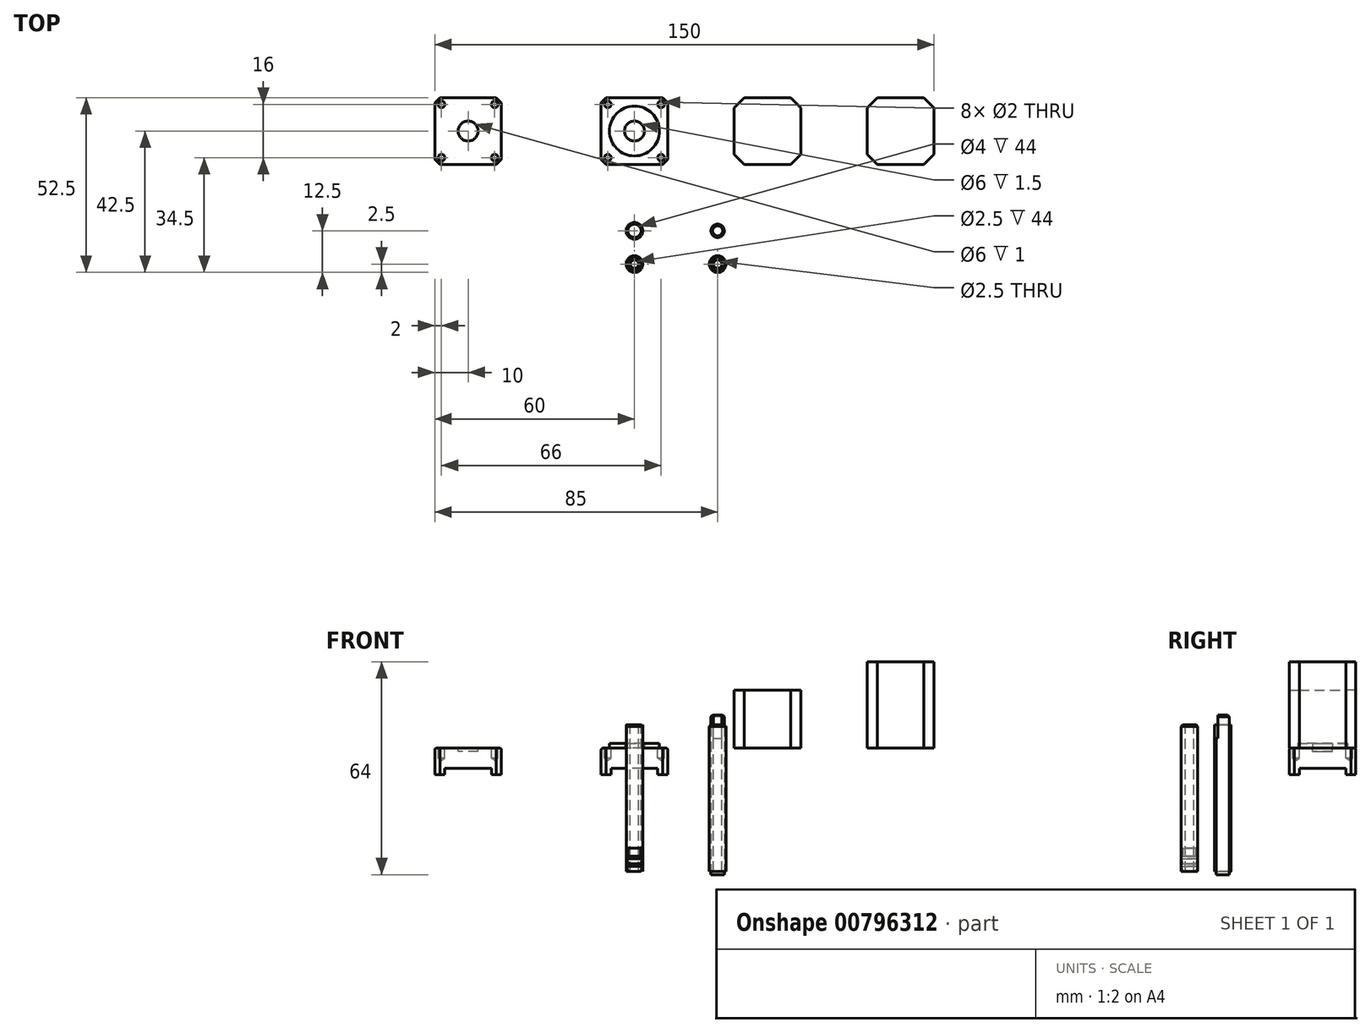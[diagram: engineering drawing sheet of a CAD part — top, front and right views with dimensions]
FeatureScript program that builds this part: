
annotation { "Feature Type Name" : "Feature", "Feature Type Description" : "" }
export const myFeature = defineFeature(function(context is Context, id is Id, definition is map)
    precondition{}
    {
        {
            var Q0;
            Q0=qCreatedBy(makeId("Top.planeOp"),FACE);
            var sketch = newSketch(context, id + "F0", { "sketchPlane" : qUnion([Q0])});
            skLineSegment(sketch, "E0.bottom", {"start": v(10, -10) * mm, "end": v(-10, -10) * mm});
            skLineSegment(sketch, "E0.top", {"start": v(10, 10) * mm, "end": v(-10, 10) * mm});
            skLineSegment(sketch, "E0.left", {"start": v(10, -10) * mm, "end": v(10, 10) * mm});
            skLineSegment(sketch, "E0.right", {"start": v(-10, -10) * mm, "end": v(-10, 10) * mm});
            skLineSegment(sketch, "E1", {"start": v(10, 10) * mm, "end": v(-10, -10) * mm, "construction": true});
            skLineSegment(sketch, "E2", {"start": v(-10, 10) * mm, "end": v(10, -10) * mm, "construction": true});
            skPoint(sketch, "E3", {"position": v(0, 0) * mm});
            skLineSegment(sketch, "E4.left", {"start": v(-8, 8) * mm, "end": v(-8, -8) * mm, "construction": true});
            skLineSegment(sketch, "E5", {"start": v(-8, 8) * mm, "end": v(8, 8) * mm, "construction": true});
            skLineSegment(sketch, "E6", {"start": v(8, 8) * mm, "end": v(8, -8) * mm, "construction": true});
            skLineSegment(sketch, "E7", {"start": v(8, -8) * mm, "end": v(-8, -8) * mm, "construction": true});
            skCircle(sketch, "E8", {"center": v(0, 0) * mm, "radius": 7.5 * mm});
            skCircle(sketch, "E9", {"center": v(0, 0) * mm, "radius": 3 * mm});
            skLineSegment(sketch, "E10", {"start": v(-7, 10) * mm, "end": v(-10, 7) * mm});
            skLineSegment(sketch, "E11", {"start": v(-8.5, 10) * mm, "end": v(-10, 8.5) * mm});
            skLineSegment(sketch, "E12", {"start": v(0, 0) * mm, "end": v(-8, 0) * mm, "construction": true});
            skLineSegment(sketch, "E13", {"start": v(0, 0) * mm, "end": v(0, 8) * mm, "construction": true});
            skLineSegment(sketch, "E14.MirrorCS", {"start": v(-7, -10) * mm, "end": v(-10, -7) * mm});
            skLineSegment(sketch, "E15.MirrorCS", {"start": v(-8.5, -10) * mm, "end": v(-10, -8.5) * mm});
            skLineSegment(sketch, "E16.MirrorCS", {"start": v(7, 10) * mm, "end": v(10, 7) * mm});
            skLineSegment(sketch, "E17.MirrorCS", {"start": v(8.5, 10) * mm, "end": v(10, 8.5) * mm});
            skLineSegment(sketch, "E18.MirrorCS", {"start": v(7, -10) * mm, "end": v(10, -7) * mm});
            skLineSegment(sketch, "E19.MirrorCS", {"start": v(8.5, -10) * mm, "end": v(10, -8.5) * mm});
            skPoint(sketch, "E20", {"position": v(-8, 8) * mm});
            skPoint(sketch, "E21", {"position": v(8, -8) * mm});
            skPoint(sketch, "E22", {"position": v(8, 8) * mm});
            skPoint(sketch, "E23", {"position": v(-8, -8) * mm});
            skLineSegment(sketch, "E24.1.0.0", {"start": v(-50, 0) * mm, "end": v(-50, 8) * mm, "construction": true});
            skCircle(sketch, "E24.1.0.1", {"center": v(-50, 0) * mm, "radius": 3 * mm});
            skLineSegment(sketch, "E24.1.0.2", {"start": v(-60, -10) * mm, "end": v(-60, 10) * mm});
            skPoint(sketch, "E24.1.0.3", {"position": v(-58, -8) * mm});
            skLineSegment(sketch, "E24.1.0.4", {"start": v(-40, -10) * mm, "end": v(-60, -10) * mm});
            skLineSegment(sketch, "E24.1.0.5", {"start": v(-58.5, -10) * mm, "end": v(-60, -8.5) * mm});
            skLineSegment(sketch, "E24.1.0.6", {"start": v(-57, -10) * mm, "end": v(-60, -7) * mm});
            skLineSegment(sketch, "E24.1.0.7", {"start": v(-43, -10) * mm, "end": v(-40, -7) * mm});
            skLineSegment(sketch, "E24.1.0.8", {"start": v(-41.5, -10) * mm, "end": v(-40, -8.5) * mm});
            skLineSegment(sketch, "E24.1.0.9", {"start": v(-40, -10) * mm, "end": v(-40, 10) * mm});
            skLineSegment(sketch, "E24.1.0.10", {"start": v(-43, 10) * mm, "end": v(-40, 7) * mm});
            skLineSegment(sketch, "E24.1.0.11", {"start": v(-41.5, 10) * mm, "end": v(-40, 8.5) * mm});
            skLineSegment(sketch, "E24.1.0.12", {"start": v(-40, 10) * mm, "end": v(-60, 10) * mm});
            skLineSegment(sketch, "E24.1.0.13", {"start": v(-57, 10) * mm, "end": v(-60, 7) * mm});
            skLineSegment(sketch, "E24.1.0.14", {"start": v(-58.5, 10) * mm, "end": v(-60, 8.5) * mm});
            skPoint(sketch, "E24.1.0.15", {"position": v(-58, 8) * mm});
            skPoint(sketch, "E24.1.0.16", {"position": v(-42, 8) * mm});
            skPoint(sketch, "E24.1.0.17", {"position": v(-42, -8) * mm});
            skLineSegment(sketch, "E24.direction1", {"start": v(0, 0) * mm, "end": v(-50, 0) * mm, "construction": true});
            skLineSegment(sketch, "E25.1.0.0", {"start": v(40, 0) * mm, "end": v(40, 8) * mm, "construction": true});
            skLineSegment(sketch, "E25.1.0.1", {"start": v(47, -10) * mm, "end": v(50, -7) * mm});
            skLineSegment(sketch, "E25.1.0.2", {"start": v(50, -10) * mm, "end": v(50, 10) * mm});
            skLineSegment(sketch, "E25.1.0.3", {"start": v(47, 10) * mm, "end": v(50, 7) * mm});
            skLineSegment(sketch, "E25.1.0.4", {"start": v(50, -10) * mm, "end": v(30, -10) * mm});
            skLineSegment(sketch, "E25.1.0.5", {"start": v(33, -10) * mm, "end": v(30, -7) * mm});
            skLineSegment(sketch, "E25.1.0.6", {"start": v(33, 10) * mm, "end": v(30, 7) * mm});
            skLineSegment(sketch, "E25.1.0.7", {"start": v(30, -10) * mm, "end": v(30, 10) * mm});
            skLineSegment(sketch, "E25.1.0.8", {"start": v(50, 10) * mm, "end": v(30, 10) * mm});
            skLineSegment(sketch, "E25.2.0.0", {"start": v(80, 0) * mm, "end": v(80, 8) * mm, "construction": true});
            skLineSegment(sketch, "E25.2.0.1", {"start": v(87, -10) * mm, "end": v(90, -7) * mm});
            skLineSegment(sketch, "E25.2.0.2", {"start": v(90, -10) * mm, "end": v(90, 10) * mm});
            skLineSegment(sketch, "E25.2.0.3", {"start": v(87, 10) * mm, "end": v(90, 7) * mm});
            skLineSegment(sketch, "E25.2.0.4", {"start": v(90, -10) * mm, "end": v(70, -10) * mm});
            skLineSegment(sketch, "E25.2.0.5", {"start": v(73, -10) * mm, "end": v(70, -7) * mm});
            skLineSegment(sketch, "E25.2.0.6", {"start": v(73, 10) * mm, "end": v(70, 7) * mm});
            skLineSegment(sketch, "E25.2.0.7", {"start": v(70, -10) * mm, "end": v(70, 10) * mm});
            skLineSegment(sketch, "E25.2.0.8", {"start": v(90, 10) * mm, "end": v(70, 10) * mm});
            skLineSegment(sketch, "E25.direction1", {"start": v(0, 0) * mm, "end": v(40, 0) * mm, "construction": true});
            skLineSegment(sketch, "E26.0.3.0", {"start": v(120, 0) * mm, "end": v(120, 8) * mm, "construction": true});
            skLineSegment(sketch, "E26.3.3.0", {"start": v(127, -10) * mm, "end": v(130, -7) * mm});
            skLineSegment(sketch, "E26.6.3.0", {"start": v(130, -10) * mm, "end": v(130, 10) * mm});
            skLineSegment(sketch, "E26.9.3.0", {"start": v(127, 10) * mm, "end": v(130, 7) * mm});
            skLineSegment(sketch, "E26.12.3.0", {"start": v(130, -10) * mm, "end": v(110, -10) * mm});
            skLineSegment(sketch, "E26.15.3.0", {"start": v(113, -10) * mm, "end": v(110, -7) * mm});
            skLineSegment(sketch, "E26.18.3.0", {"start": v(113, 10) * mm, "end": v(110, 7) * mm});
            skLineSegment(sketch, "E26.21.3.0", {"start": v(110, -10) * mm, "end": v(110, 10) * mm});
            skLineSegment(sketch, "E26.24.3.0", {"start": v(130, 10) * mm, "end": v(110, 10) * mm});
            skLineSegment(sketch, "E27.0.4.0", {"start": v(160, 0) * mm, "end": v(160, 8) * mm, "construction": true});
            skLineSegment(sketch, "E27.3.4.0", {"start": v(167, -10) * mm, "end": v(170, -7) * mm});
            skLineSegment(sketch, "E27.6.4.0", {"start": v(170, -10) * mm, "end": v(170, 10) * mm});
            skLineSegment(sketch, "E27.9.4.0", {"start": v(167, 10) * mm, "end": v(170, 7) * mm});
            skLineSegment(sketch, "E27.12.4.0", {"start": v(170, -10) * mm, "end": v(150, -10) * mm});
            skLineSegment(sketch, "E27.15.4.0", {"start": v(153, -10) * mm, "end": v(150, -7) * mm});
            skLineSegment(sketch, "E27.18.4.0", {"start": v(153, 10) * mm, "end": v(150, 7) * mm});
            skLineSegment(sketch, "E27.21.4.0", {"start": v(150, -10) * mm, "end": v(150, 10) * mm});
            skLineSegment(sketch, "E27.24.4.0", {"start": v(170, 10) * mm, "end": v(150, 10) * mm});
            skCircle(sketch, "E28", {"center": v(0, -30) * mm, "radius": 2.5 * mm});
            skCircle(sketch, "E29", {"center": v(0, -40) * mm, "radius": 2.5 * mm});
            skLineSegment(sketch, "E30", {"start": v(1.5, -42) * mm, "end": v(-1.5, -42) * mm});
            skLineSegment(sketch, "E31", {"start": v(1.5, -32) * mm, "end": v(-1.5, -32) * mm});
            skCircle(sketch, "E32.1.0.0", {"center": v(25, -40) * mm, "radius": 2.5 * mm});
            skCircle(sketch, "E32.1.0.1", {"center": v(25, -30) * mm, "radius": 2.5 * mm});
            skLineSegment(sketch, "E32.1.0.2", {"start": v(26.5, -32) * mm, "end": v(23.5, -32) * mm});
            skLineSegment(sketch, "E32.1.0.3", {"start": v(26.5, -42) * mm, "end": v(23.5, -42) * mm});
            skCircle(sketch, "E32.2.0.0", {"center": v(50, -40) * mm, "radius": 2.5 * mm});
            skCircle(sketch, "E32.2.0.1", {"center": v(50, -30) * mm, "radius": 2.5 * mm});
            skLineSegment(sketch, "E32.2.0.2", {"start": v(51.5, -32) * mm, "end": v(48.5, -32) * mm});
            skLineSegment(sketch, "E32.2.0.3", {"start": v(51.5, -42) * mm, "end": v(48.5, -42) * mm});
            skCircle(sketch, "E32.3.0.0", {"center": v(75, -40) * mm, "radius": 2.5 * mm});
            skCircle(sketch, "E32.3.0.1", {"center": v(75, -30) * mm, "radius": 2.5 * mm});
            skLineSegment(sketch, "E32.3.0.2", {"start": v(76.5, -32) * mm, "end": v(73.5, -32) * mm});
            skLineSegment(sketch, "E32.3.0.3", {"start": v(76.5, -42) * mm, "end": v(73.5, -42) * mm});
            skCircle(sketch, "E32.4.0.0", {"center": v(100, -40) * mm, "radius": 2.5 * mm});
            skCircle(sketch, "E32.4.0.1", {"center": v(100, -30) * mm, "radius": 2.5 * mm});
            skLineSegment(sketch, "E32.4.0.2", {"start": v(101.5, -32) * mm, "end": v(98.5, -32) * mm});
            skLineSegment(sketch, "E32.4.0.3", {"start": v(101.5, -42) * mm, "end": v(98.5, -42) * mm});
            skLineSegment(sketch, "E32.direction1", {"start": v(0, -40) * mm, "end": v(25, -40) * mm, "construction": true});
            skSolve(sketch);
        }
        {
            var Q0;
            Q0=makeQuery(id+"F0.imprint","IMPRINT",FACE,{"disambiguationData":[TD([[makeQuery(id+"F0.imprint","IMPRINT",EDGE,{"derivedFrom":sQuery(id+"F0.wireOp",EDGE,"E24.1.0.1")}),-1.0]])]});
            var Q1;
            Q1=makeQuery(id+"F0.imprint","IMPRINT",FACE,{"disambiguationData":[TD([[makeQuery(id+"F0.imprint","IMPRINT",EDGE,{"derivedFrom":sQuery(id+"F0.wireOp",EDGE,"E8")}),-1.0]])]});
            var Q2;
            Q2=makeQuery(id+"F0.imprint","IMPRINT",FACE,{"disambiguationData":[TD([[makeQuery(id+"F0.imprint","IMPRINT",EDGE,{"derivedFrom":sQuery(id+"F0.wireOp",EDGE,"E8")}),1.0]])]});
            var Q3;
            {var subQ0=sQuery(id+"F0.wireOp",EDGE,"E24.1.0.10");Q3=makeQuery(id+"F0.imprint","IMPRINT",FACE,{"disambiguationData":[TD([[makeQuery(id+"F0.imprint","IMPRINT",EDGE,{"derivedFrom":subQ0}),1.0]])]});}
            var Q4;
            {var subQ0=sQuery(id+"F0.wireOp",EDGE,"E24.1.0.13");Q4=makeQuery(id+"F0.imprint","IMPRINT",FACE,{"disambiguationData":[TD([[makeQuery(id+"F0.imprint","IMPRINT",EDGE,{"derivedFrom":subQ0}),-1.0]])]});}
            var Q5;
            {var subQ0=sQuery(id+"F0.wireOp",EDGE,"E24.1.0.5");Q5=makeQuery(id+"F0.imprint","IMPRINT",FACE,{"disambiguationData":[TD([[makeQuery(id+"F0.imprint","IMPRINT",EDGE,{"derivedFrom":subQ0}),-1.0]])]});}
            var Q6;
            {var subQ0=sQuery(id+"F0.wireOp",EDGE,"E24.1.0.7");Q6=makeQuery(id+"F0.imprint","IMPRINT",FACE,{"disambiguationData":[TD([[makeQuery(id+"F0.imprint","IMPRINT",EDGE,{"derivedFrom":subQ0}),-1.0]])]});}
            var Q7;
            {var subQ0=sQuery(id+"F0.wireOp",EDGE,"E14.MirrorCS");Q7=makeQuery(id+"F0.imprint","IMPRINT",FACE,{"disambiguationData":[TD([[makeQuery(id+"F0.imprint","IMPRINT",EDGE,{"derivedFrom":subQ0}),1.0]])]});}
            var Q8;
            {var subQ0=sQuery(id+"F0.wireOp",EDGE,"E10");Q8=makeQuery(id+"F0.imprint","IMPRINT",FACE,{"disambiguationData":[TD([[makeQuery(id+"F0.imprint","IMPRINT",EDGE,{"derivedFrom":subQ0}),-1.0]])]});}
            var Q9;
            {var subQ0=sQuery(id+"F0.wireOp",EDGE,"E16.MirrorCS");Q9=makeQuery(id+"F0.imprint","IMPRINT",FACE,{"disambiguationData":[TD([[makeQuery(id+"F0.imprint","IMPRINT",EDGE,{"derivedFrom":subQ0}),1.0]])]});}
            var Q10;
            {var subQ0=sQuery(id+"F0.wireOp",EDGE,"E18.MirrorCS");Q10=makeQuery(id+"F0.imprint","IMPRINT",FACE,{"disambiguationData":[TD([[makeQuery(id+"F0.imprint","IMPRINT",EDGE,{"derivedFrom":subQ0}),-1.0]])]});}
            var Q11;
            Q11=makeQuery(id+"F0.imprint","IMPRINT",FACE,{"disambiguationData":[TD([[makeQuery(id+"F0.imprint","IMPRINT",EDGE,{"derivedFrom":sQuery(id+"F0.wireOp",EDGE,"E9")}),1.0]])]});
            var Q12;
            Q12=makeQuery(id+"F0.imprint","IMPRINT",FACE,{"disambiguationData":[TD([[makeQuery(id+"F0.imprint","IMPRINT",EDGE,{"derivedFrom":sQuery(id+"F0.wireOp",EDGE,"E24.1.0.1")}),1.0]])]});
            extrude(context, id + "F1", {"entities" : qUnion([Q0, Q1, Q2, Q3, Q4, Q5, Q6, Q7, Q8, Q9, Q10, Q11, Q12]), "oppositeDirection" : true, "depth" : 6 * mm, "offsetDistance" : 25 * mm});
        }
        {
            var Q0;
            Q0=makeQuery(id+"F0.imprint","IMPRINT",FACE,{"disambiguationData":[TD([[makeQuery(id+"F0.imprint","IMPRINT",EDGE,{"derivedFrom":sQuery(id+"F0.wireOp",EDGE,"E8")}),1.0]])]});
            extrude(context, id + "F2", {"entities" : qUnion([Q0]), "operationType" : NewBodyOperationType.ADD, "depth" : 1.5 * mm, "offsetDistance" : 25 * mm});
        }
        {
            var Q0;
            Q0=makeQuery(id+"F0.imprint","IMPRINT",FACE,{"disambiguationData":[TD([[makeQuery(id+"F0.imprint","IMPRINT",EDGE,{"derivedFrom":sQuery(id+"F0.wireOp",EDGE,"E24.1.0.1")}),1.0]])]});
            extrude(context, id + "F3", {"entities" : qUnion([Q0]), "operationType" : NewBodyOperationType.REMOVE, "oppositeDirection" : true, "depth" : 1 * mm, "offsetDistance" : 25 * mm});
        }
        {
            var Q0;
            Q0=makeQuery(id+"F1.opExtrude","CAP_FACE",FACE,{"disambiguationData":[OSD([sQuery(id+"F0.wireOp",EDGE,"E0.bottom"),sQuery(id+"F0.wireOp",EDGE,"E0.top"),sQuery(id+"F0.wireOp",EDGE,"E0.left"),sQuery(id+"F0.wireOp",EDGE,"E0.right"),sQuery(id+"F0.wireOp",EDGE,"E11"),sQuery(id+"F0.wireOp",EDGE,"E15.MirrorCS"),sQuery(id+"F0.wireOp",EDGE,"E17.MirrorCS"),sQuery(id+"F0.wireOp",EDGE,"E19.MirrorCS")])],"isStart":false});
            var sketch = newSketch(context, id + "F4", { "sketchPlane" : qUnion([Q0])});
            skLineSegment(sketch, "E33.0", {"start": v(7, -10) * mm, "end": v(10, -7) * mm});
            skLineSegment(sketch, "E33.1", {"start": v(8.5, -10) * mm, "end": v(10, -8.5) * mm});
            skLineSegment(sketch, "E33.2", {"start": v(10, 8.5) * mm, "end": v(10, 7) * mm});
            skLineSegment(sketch, "E33.3", {"start": v(8.5, -10) * mm, "end": v(7, -10) * mm});
            skLineSegment(sketch, "E33.4", {"start": v(-7, -10) * mm, "end": v(-10, -7) * mm});
            skLineSegment(sketch, "E33.5", {"start": v(-8.5, -10) * mm, "end": v(-10, -8.5) * mm});
            skLineSegment(sketch, "E33.6", {"start": v(-10, 8.5) * mm, "end": v(-10, 7) * mm});
            skLineSegment(sketch, "E33.7", {"start": v(8.5, 10) * mm, "end": v(10, 8.5) * mm});
            skLineSegment(sketch, "E33.8", {"start": v(7, 10) * mm, "end": v(10, 7) * mm});
            skLineSegment(sketch, "E33.9", {"start": v(8.5, 10) * mm, "end": v(7, 10) * mm});
            skLineSegment(sketch, "E33.10", {"start": v(-7, 10) * mm, "end": v(-10, 7) * mm});
            skLineSegment(sketch, "E33.11", {"start": v(-8.5, 10) * mm, "end": v(-10, 8.5) * mm});
            skPoint(sketch, "E34.orphan", {"position": v(10, -10) * mm});
            skPoint(sketch, "E35.orphan", {"position": v(-10, -10) * mm});
            skLineSegment(sketch, "E36.trimOffspring", {"start": v(-10, -7) * mm, "end": v(-10, -8.5) * mm});
            skLineSegment(sketch, "E37.trimOffspring", {"start": v(-7, 10) * mm, "end": v(-8.5, 10) * mm});
            skLineSegment(sketch, "E38.trimOffspring", {"start": v(10, -7) * mm, "end": v(10, -8.5) * mm});
            skPoint(sketch, "E39.orphan", {"position": v(10, 10) * mm});
            skLineSegment(sketch, "E40.trimOffspring", {"start": v(-7, -10) * mm, "end": v(-8.5, -10) * mm});
            skPoint(sketch, "E41.orphan", {"position": v(-10, 10) * mm});
            skLineSegment(sketch, "E42.0", {"start": v(-40, 8.5) * mm, "end": v(-40, 7) * mm});
            skLineSegment(sketch, "E42.1", {"start": v(-43, -10) * mm, "end": v(-40, -7) * mm});
            skLineSegment(sketch, "E42.2", {"start": v(-41.5, -10) * mm, "end": v(-40, -8.5) * mm});
            skLineSegment(sketch, "E42.3", {"start": v(-41.5, -10) * mm, "end": v(-43, -10) * mm});
            skLineSegment(sketch, "E42.4", {"start": v(-41.5, 10) * mm, "end": v(-40, 8.5) * mm});
            skLineSegment(sketch, "E42.5", {"start": v(-43, 10) * mm, "end": v(-40, 7) * mm});
            skLineSegment(sketch, "E42.6", {"start": v(-41.5, 10) * mm, "end": v(-58.5, 10) * mm});
            skLineSegment(sketch, "E42.7", {"start": v(-57, -10) * mm, "end": v(-60, -7) * mm});
            skLineSegment(sketch, "E42.8", {"start": v(-58.5, -10) * mm, "end": v(-60, -8.5) * mm});
            skLineSegment(sketch, "E42.9", {"start": v(-60, 8.5) * mm, "end": v(-60, 7) * mm});
            skLineSegment(sketch, "E42.10", {"start": v(-58.5, 10) * mm, "end": v(-60, 8.5) * mm});
            skLineSegment(sketch, "E42.11", {"start": v(-57, 10) * mm, "end": v(-60, 7) * mm});
            skPoint(sketch, "E43.orphan", {"position": v(-40, -10) * mm});
            skLineSegment(sketch, "E44.trimOffspring", {"start": v(-57, -10) * mm, "end": v(-58.5, -10) * mm});
            skPoint(sketch, "E45.orphan", {"position": v(-60, -10) * mm});
            skLineSegment(sketch, "E46.trimOffspring", {"start": v(-60, -7) * mm, "end": v(-60, -8.5) * mm});
            skLineSegment(sketch, "E47.trimOffspring", {"start": v(-40, -7) * mm, "end": v(-40, -8.5) * mm});
            skPoint(sketch, "E48.orphan", {"position": v(-40, 10) * mm});
            skPoint(sketch, "E49.orphan", {"position": v(-60, 10) * mm});
            skSolve(sketch);
        }
        {
            var Q0;
            Q0=makeQuery(id+"F4.imprint","IMPRINT",FACE,{"disambiguationData":[TD([[makeQuery(id+"F4.imprint","IMPRINT",EDGE,{"derivedFrom":sQuery(id+"F4.wireOp",EDGE,"E42.1")}),-1.0]])]});
            var Q1;
            Q1=makeQuery(id+"F4.imprint","IMPRINT",FACE,{"disambiguationData":[TD([[makeQuery(id+"F4.imprint","IMPRINT",EDGE,{"derivedFrom":sQuery(id+"F4.wireOp",EDGE,"E42.7")}),1.0]])]});
            var Q2;
            Q2=makeQuery(id+"F4.imprint","IMPRINT",FACE,{"disambiguationData":[TD([[makeQuery(id+"F4.imprint","IMPRINT",EDGE,{"derivedFrom":sQuery(id+"F4.wireOp",EDGE,"E42.9")}),1.0]])]});
            var Q3;
            Q3=makeQuery(id+"F4.imprint","IMPRINT",FACE,{"disambiguationData":[TD([[makeQuery(id+"F4.imprint","IMPRINT",EDGE,{"derivedFrom":sQuery(id+"F4.wireOp",EDGE,"E42.0")}),-1.0]])]});
            var Q4;
            Q4=makeQuery(id+"F4.imprint","IMPRINT",FACE,{"disambiguationData":[TD([[makeQuery(id+"F4.imprint","IMPRINT",EDGE,{"derivedFrom":sQuery(id+"F4.wireOp",EDGE,"E33.4")}),1.0]])]});
            var Q5;
            Q5=makeQuery(id+"F4.imprint","IMPRINT",FACE,{"disambiguationData":[TD([[makeQuery(id+"F4.imprint","IMPRINT",EDGE,{"derivedFrom":sQuery(id+"F4.wireOp",EDGE,"E33.0")}),-1.0]])]});
            var Q6;
            Q6=makeQuery(id+"F4.imprint","IMPRINT",FACE,{"disambiguationData":[TD([[makeQuery(id+"F4.imprint","IMPRINT",EDGE,{"derivedFrom":sQuery(id+"F4.wireOp",EDGE,"E33.2")}),-1.0]])]});
            var Q7;
            Q7=makeQuery(id+"F4.imprint","IMPRINT",FACE,{"disambiguationData":[TD([[makeQuery(id+"F4.imprint","IMPRINT",EDGE,{"derivedFrom":sQuery(id+"F4.wireOp",EDGE,"E33.6")}),1.0]])]});
            extrude(context, id + "F5", {"entities" : qUnion([Q0, Q1, Q2, Q3, Q4, Q5, Q6, Q7]), "operationType" : NewBodyOperationType.ADD, "depth" : 2 * mm, "offsetDistance" : 25 * mm});
        }
        {
            var Q0;
            Q0=sQuery(id+"F0.wireOp",VERTEX,"E23");
            var Q1;
            Q1=sQuery(id+"F0.wireOp",VERTEX,"E21");
            var Q2;
            Q2=sQuery(id+"F0.wireOp",VERTEX,"E22");
            var Q3;
            Q3=sQuery(id+"F0.wireOp",VERTEX,"E20");
            var Q4;
            Q4=sQuery(id+"F0.wireOp",VERTEX,"E24.1.0.17");
            var Q5;
            Q5=sQuery(id+"F0.wireOp",VERTEX,"E24.1.0.16");
            var Q6;
            Q6=sQuery(id+"F0.wireOp",VERTEX,"E24.1.0.15");
            var Q7;
            Q7=sQuery(id+"F0.wireOp",VERTEX,"E24.1.0.3");
            var Q8;
            Q8=makeQuery(id+"F1.opExtrude","SWEPT_BODY",BODY,{"disambiguationData":[OSD([sQuery(id+"F0.wireOp",EDGE,"E0.bottom"),sQuery(id+"F0.wireOp",EDGE,"E0.top"),sQuery(id+"F0.wireOp",EDGE,"E0.left"),sQuery(id+"F0.wireOp",EDGE,"E0.right"),sQuery(id+"F0.wireOp",EDGE,"E11"),sQuery(id+"F0.wireOp",EDGE,"E15.MirrorCS"),sQuery(id+"F0.wireOp",EDGE,"E17.MirrorCS"),sQuery(id+"F0.wireOp",EDGE,"E19.MirrorCS")])]});
            var Q9;
            Q9=makeQuery(id+"F1.opExtrude","SWEPT_BODY",BODY,{"disambiguationData":[OSD([sQuery(id+"F0.wireOp",EDGE,"E24.1.0.2"),sQuery(id+"F0.wireOp",EDGE,"E24.1.0.4"),sQuery(id+"F0.wireOp",EDGE,"E24.1.0.5"),sQuery(id+"F0.wireOp",EDGE,"E24.1.0.8"),sQuery(id+"F0.wireOp",EDGE,"E24.1.0.9"),sQuery(id+"F0.wireOp",EDGE,"E24.1.0.11"),sQuery(id+"F0.wireOp",EDGE,"E24.1.0.12"),sQuery(id+"F0.wireOp",EDGE,"E24.1.0.14")])]});
            hole(context, id + "F6", {"style" : HoleStyle.SIMPLE, "endStyle" : HoleEndStyle.BLIND, "holeDiameter" : 2 * mm, "majorDiameter" : 5 * mm, "holeDepth" : 3 * mm, "isTappedThrough" : true, "tappedDepth" : 3.5 * mm, "tapClearance" : 3, "locations" : qUnion([Q0, Q1, Q2, Q3, Q4, Q5, Q6, Q7]), "scope" : qUnion([Q8, Q9])});
        }
        {
            var Q0;
            {var subQ1=sQuery(id+"F0.wireOp",EDGE,"E25.1.0.1");Q0=makeQuery(id+"F0.imprint","IMPRINT",FACE,{"disambiguationData":[TD([[makeQuery(id+"F0.imprint","IMPRINT",EDGE,{"derivedFrom":subQ1}),1.0]])]});}
            extrude(context, id + "F7", {"entities" : qUnion([Q0]), "depth" : (38 - 8.5 - 2 * 6) * mm, "offsetDistance" : 25 * mm});
        }
        {
            var Q0;
            {var subQ0=sQuery(id+"F0.wireOp",EDGE,"E31");Q0=makeQuery(id+"F0.imprint","IMPRINT",FACE,{"disambiguationData":[TD([[makeQuery(id+"F0.imprint","IMPRINT",EDGE,{"derivedFrom":subQ0}),-1.0]])]});}
            var Q1;
            {var subQ0=sQuery(id+"F0.wireOp",EDGE,"E30");Q1=makeQuery(id+"F0.imprint","IMPRINT",FACE,{"disambiguationData":[TD([[makeQuery(id+"F0.imprint","IMPRINT",EDGE,{"derivedFrom":subQ0}),-1.0]])]});}
            var Q2;
            {var subQ0=sQuery(id+"F0.wireOp",EDGE,"E32.1.0.3");Q2=makeQuery(id+"F0.imprint","IMPRINT",FACE,{"disambiguationData":[TD([[makeQuery(id+"F0.imprint","IMPRINT",EDGE,{"derivedFrom":subQ0}),-1.0]])]});}
            var Q3;
            {var subQ0=sQuery(id+"F0.wireOp",EDGE,"E30");Q3=makeQuery(id+"F0.imprint","IMPRINT",FACE,{"disambiguationData":[TD([[makeQuery(id+"F0.imprint","IMPRINT",EDGE,{"derivedFrom":subQ0}),1.0]])]});}
            var Q4;
            {var subQ0=sQuery(id+"F0.wireOp",EDGE,"E31");Q4=makeQuery(id+"F0.imprint","IMPRINT",FACE,{"disambiguationData":[TD([[makeQuery(id+"F0.imprint","IMPRINT",EDGE,{"derivedFrom":subQ0}),1.0]])]});}
            var Q5;
            {var subQ0=sQuery(id+"F0.wireOp",EDGE,"E32.1.0.3");Q5=makeQuery(id+"F0.imprint","IMPRINT",FACE,{"disambiguationData":[TD([[makeQuery(id+"F0.imprint","IMPRINT",EDGE,{"derivedFrom":subQ0}),1.0]])]});}
            extrude(context, id + "F8", {"entities" : qUnion([Q0, Q1, Q2, Q3, Q4, Q5]), "depth" : 7 * mm, "offsetDistance" : 25 * mm});
        }
        {
            var Q0;
            Q0=makeQuery(id+"F1.opExtrude","CAP_EDGE",EDGE,{"disambiguationData":[OSD([sQuery(id+"F0.wireOp",EDGE,"E24.1.0.9")])],"isStart":true});
            var Q1;
            Q1=makeQuery(id+"F1.opExtrude","CAP_EDGE",EDGE,{"disambiguationData":[OSD([sQuery(id+"F0.wireOp",EDGE,"E24.1.0.8")])],"isStart":true});
            var Q2;
            Q2=makeQuery(id+"F1.opExtrude","CAP_EDGE",EDGE,{"disambiguationData":[OSD([sQuery(id+"F0.wireOp",EDGE,"E24.1.0.5")])],"isStart":true});
            var Q3;
            Q3=makeQuery(id+"F1.opExtrude","CAP_EDGE",EDGE,{"disambiguationData":[OSD([sQuery(id+"F0.wireOp",EDGE,"E24.1.0.2")])],"isStart":true});
            var Q4;
            Q4=makeQuery(id+"F1.opExtrude","CAP_EDGE",EDGE,{"disambiguationData":[OSD([sQuery(id+"F0.wireOp",EDGE,"E24.1.0.4")])],"isStart":true});
            var Q5;
            Q5=makeQuery(id+"F1.opExtrude","CAP_EDGE",EDGE,{"disambiguationData":[OSD([sQuery(id+"F0.wireOp",EDGE,"E24.1.0.12")])],"isStart":true});
            var Q6;
            Q6=makeQuery(id+"F1.opExtrude","CAP_EDGE",EDGE,{"disambiguationData":[OSD([sQuery(id+"F0.wireOp",EDGE,"E24.1.0.11")])],"isStart":true});
            var Q7;
            Q7=makeQuery(id+"F1.opExtrude","CAP_EDGE",EDGE,{"disambiguationData":[OSD([sQuery(id+"F0.wireOp",EDGE,"E24.1.0.14")])],"isStart":true});
            var Q8;
            Q8=makeQuery(id+"F1.opExtrude","CAP_EDGE",EDGE,{"disambiguationData":[OSD([sQuery(id+"F0.wireOp",EDGE,"E0.right")])],"isStart":true});
            var Q9;
            Q9=makeQuery(id+"F1.opExtrude","CAP_EDGE",EDGE,{"disambiguationData":[OSD([sQuery(id+"F0.wireOp",EDGE,"E15.MirrorCS")])],"isStart":true});
            var Q10;
            Q10=makeQuery(id+"F1.opExtrude","CAP_EDGE",EDGE,{"disambiguationData":[OSD([sQuery(id+"F0.wireOp",EDGE,"E0.bottom")])],"isStart":true});
            var Q11;
            Q11=makeQuery(id+"F1.opExtrude","CAP_EDGE",EDGE,{"disambiguationData":[OSD([sQuery(id+"F0.wireOp",EDGE,"E19.MirrorCS")])],"isStart":true});
            var Q12;
            Q12=makeQuery(id+"F1.opExtrude","CAP_EDGE",EDGE,{"disambiguationData":[OSD([sQuery(id+"F0.wireOp",EDGE,"E0.left")])],"isStart":true});
            var Q13;
            Q13=makeQuery(id+"F1.opExtrude","CAP_EDGE",EDGE,{"disambiguationData":[OSD([sQuery(id+"F0.wireOp",EDGE,"E17.MirrorCS")])],"isStart":true});
            var Q14;
            Q14=makeQuery(id+"F1.opExtrude","CAP_EDGE",EDGE,{"disambiguationData":[OSD([sQuery(id+"F0.wireOp",EDGE,"E0.top")])],"isStart":true});
            var Q15;
            Q15=makeQuery(id+"F1.opExtrude","CAP_EDGE",EDGE,{"disambiguationData":[OSD([sQuery(id+"F0.wireOp",EDGE,"E11")])],"isStart":true});
            fillet(context, id + "F9", {"entities" : qUnion([Q0, Q1, Q2, Q3, Q4, Q5, Q6, Q7, Q8, Q9, Q10, Q11, Q12, Q13, Q14, Q15]), "radius" : 0.5 * mm, "tangentPropagation" : true, "allowEdgeOverflow" : false});
        }
        {
            var Q0;
            Q0=makeQuery(id+"F8.opExtrude","CAP_EDGE",EDGE,{"disambiguationData":[OSD([sQuery(id+"F0.wireOp",EDGE,"E29")])],"isStart":false});
            var Q1;
            Q1=makeQuery(id+"F8.opExtrude","CAP_EDGE",EDGE,{"disambiguationData":[OSD([sQuery(id+"F0.wireOp",EDGE,"E32.1.0.1")])],"isStart":false});
            var Q2;
            Q2=makeQuery(id+"F8.opExtrude","CAP_EDGE",EDGE,{"disambiguationData":[OSD([sQuery(id+"F0.wireOp",EDGE,"E32.1.0.0")])],"isStart":false});
            var Q3;
            Q3=makeQuery(id+"F8.opExtrude","CAP_EDGE",EDGE,{"disambiguationData":[OSD([sQuery(id+"F0.wireOp",EDGE,"E32.2.0.0")])],"isStart":false});
            var Q4;
            Q4=makeQuery(id+"F8.opExtrude","CAP_EDGE",EDGE,{"disambiguationData":[OSD([sQuery(id+"F0.wireOp",EDGE,"E32.2.0.1")])],"isStart":false});
            var Q5;
            Q5=makeQuery(id+"F8.opExtrude","CAP_EDGE",EDGE,{"disambiguationData":[OSD([sQuery(id+"F0.wireOp",EDGE,"E32.3.0.1")])],"isStart":false});
            var Q6;
            Q6=makeQuery(id+"F8.opExtrude","CAP_EDGE",EDGE,{"disambiguationData":[OSD([sQuery(id+"F0.wireOp",EDGE,"E32.3.0.0")])],"isStart":false});
            var Q7;
            Q7=makeQuery(id+"F8.opExtrude","CAP_EDGE",EDGE,{"disambiguationData":[OSD([sQuery(id+"F0.wireOp",EDGE,"E32.4.0.0")])],"isStart":false});
            var Q8;
            Q8=makeQuery(id+"F8.opExtrude","CAP_EDGE",EDGE,{"disambiguationData":[OSD([sQuery(id+"F0.wireOp",EDGE,"E32.4.0.1")])],"isStart":false});
            chamfer(context, id + "F10", {"entities" : qUnion([Q0, Q1, Q2, Q3, Q4, Q5, Q6, Q7, Q8]), "width" : 0.5 * mm});
        }
        {
            var Q0;
            Q0=makeQuery(id+"F8.opExtrude","CAP_FACE",FACE,{"disambiguationData":[OSD([sQuery(id+"F0.wireOp",EDGE,"E29")])],"isStart":true});
            var Q1;
            Q1=makeQuery(id+"F8.opExtrude","CAP_FACE",FACE,{"disambiguationData":[OSD([sQuery(id+"F0.wireOp",EDGE,"E28")])],"isStart":true});
            var Q2;
            Q2=makeQuery(id+"F8.opExtrude","CAP_FACE",FACE,{"disambiguationData":[OSD([sQuery(id+"F0.wireOp",EDGE,"E32.1.0.0")])],"isStart":true});
            extrude(context, id + "F11", {"entities" : qUnion([Q0, Q1, Q2]), "operationType" : NewBodyOperationType.ADD, "depth" : 37 * mm, "offsetDistance" : 25 * mm});
        }
        {
            var Q0;
            Q0=makeQuery(id+"F8.opExtrude","CAP_FACE",FACE,{"disambiguationData":[OSD([sQuery(id+"F0.wireOp",EDGE,"E29")])],"isStart":false});
            var sketch = newSketch(context, id + "F12", { "sketchPlane" : qUnion([Q0])});
            skCircle(sketch, "E50", {"center": v(0, -40) * mm, "radius": 1.25 * mm});
            skCircle(sketch, "E51", {"center": v(0, -30) * mm, "radius": 2 * mm});
            skCircle(sketch, "E52", {"center": v(25, -40) * mm, "radius": 1.25 * mm});
            skSolve(sketch);
        }
        {
            var Q0;
            Q0=makeQuery(id+"F12.imprint","IMPRINT",FACE,{"disambiguationData":[TD([[makeQuery(id+"F12.imprint","IMPRINT",EDGE,{"derivedFrom":sQuery(id+"F12.wireOp",EDGE,"E50")}),1.0]])]});
            var Q1;
            Q1=makeQuery(id+"F12.imprint","IMPRINT",FACE,{"disambiguationData":[TD([[makeQuery(id+"F12.imprint","IMPRINT",EDGE,{"derivedFrom":sQuery(id+"F12.wireOp",EDGE,"E51")}),1.0]])]});
            var Q2;
            Q2=makeQuery(id+"F12.imprint","IMPRINT",FACE,{"disambiguationData":[TD([[makeQuery(id+"F12.imprint","IMPRINT",EDGE,{"derivedFrom":sQuery(id+"F12.wireOp",EDGE,"E52")}),1.0]])]});
            extrude(context, id + "F13", {"entities" : qUnion([Q0, Q1, Q2]), "operationType" : NewBodyOperationType.REMOVE, "endBound" : BoundingType.THROUGH_ALL, "oppositeDirection" : true, "depth" : 25 * mm, "offsetDistance" : 25 * mm});
        }
        {
            var Q0;
            Q0=qCreatedBy(makeId("Right.planeOp"),FACE);
            var sketch = newSketch(context, id + "F14", { "sketchPlane" : qUnion([Q0])});
            skLineSegment(sketch, "E53.0", {"start": v(-42.5, -37) * mm, "end": v(-37.5, -37) * mm});
            skLineSegment(sketch, "E54", {"start": v(-40, -37) * mm, "end": v(-40, -30) * mm, "construction": true});
            skLineSegment(sketch, "E55", {"start": v(-40, -30) * mm, "end": v(-42.5, -30) * mm});
            skLineSegment(sketch, "E56", {"start": v(-41.9, -30) * mm, "end": v(-41.9, -37) * mm});
            skLineSegment(sketch, "E57", {"start": v(-41.9, -37) * mm, "end": v(-42.4, -35.5) * mm});
            skLineSegment(sketch, "E58", {"start": v(-42.4, -35.5) * mm, "end": v(-42.4, -34.7) * mm});
            skLineSegment(sketch, "E59", {"start": v(-42.4, -34.7) * mm, "end": v(-41.9, -34.7) * mm});
            skLineSegment(sketch, "E60", {"start": v(-42.5, -30) * mm, "end": v(-42.5, -37) * mm});
            skLineSegment(sketch, "E61.0.1.0", {"start": v(-41.9, -34.7) * mm, "end": v(-42.4, -33.2) * mm});
            skLineSegment(sketch, "E61.0.1.1", {"start": v(-42.4, -33.2) * mm, "end": v(-42.4, -32.4) * mm});
            skLineSegment(sketch, "E61.0.1.2", {"start": v(-42.4, -32.4) * mm, "end": v(-41.9, -32.4) * mm});
            skLineSegment(sketch, "E61.1.0.0", {"start": v(-16.9, -37) * mm, "end": v(-17.4, -35.5) * mm});
            skLineSegment(sketch, "E61.1.0.1", {"start": v(-17.4, -35.5) * mm, "end": v(-17.4, -34.7) * mm});
            skLineSegment(sketch, "E61.1.0.2", {"start": v(-17.4, -34.7) * mm, "end": v(-16.9, -34.7) * mm});
            skLineSegment(sketch, "E61.1.1.0", {"start": v(-16.9, -34.7) * mm, "end": v(-17.4, -33.2) * mm});
            skLineSegment(sketch, "E61.1.1.1", {"start": v(-17.4, -33.2) * mm, "end": v(-17.4, -32.4) * mm});
            skLineSegment(sketch, "E61.1.1.2", {"start": v(-17.4, -32.4) * mm, "end": v(-16.9, -32.4) * mm});
            skLineSegment(sketch, "E61.2.0.0", {"start": v(8.1, -37) * mm, "end": v(7.6, -35.5) * mm});
            skLineSegment(sketch, "E61.2.0.1", {"start": v(7.6, -35.5) * mm, "end": v(7.6, -34.7) * mm});
            skLineSegment(sketch, "E61.2.0.2", {"start": v(7.6, -34.7) * mm, "end": v(8.1, -34.7) * mm});
            skLineSegment(sketch, "E61.2.1.0", {"start": v(8.1, -34.7) * mm, "end": v(7.6, -33.2) * mm});
            skLineSegment(sketch, "E61.2.1.1", {"start": v(7.6, -33.2) * mm, "end": v(7.6, -32.4) * mm});
            skLineSegment(sketch, "E61.2.1.2", {"start": v(7.6, -32.4) * mm, "end": v(8.1, -32.4) * mm});
            skLineSegment(sketch, "E61.direction1", {"start": v(-41.9, -37) * mm, "end": v(-16.9, -37) * mm, "construction": true});
            skLineSegment(sketch, "E61.direction2", {"start": v(-41.9, -37) * mm, "end": v(-41.9, -34.7) * mm, "construction": true});
            skLineSegment(sketch, "E62", {"start": v(-42.4, -32.4) * mm, "end": v(-42.5, -32.4) * mm});
            skSolve(sketch);
        }
        {
            var Q0;
            {var subQ4=sQuery(id+"F14.wireOp",EDGE,"E61.0.1.2");Q0=makeQuery(id+"F14.imprint","IMPRINT",FACE,{"disambiguationData":[TD([[makeQuery(id+"F14.imprint","IMPRINT",EDGE,{"derivedFrom":subQ4}),1.0]])]});}
            var Q1;
            {var subQ0=sQuery(id+"F14.wireOp",EDGE,"E57");Q1=makeQuery(id+"F14.imprint","IMPRINT",FACE,{"disambiguationData":[TD([[makeQuery(id+"F14.imprint","IMPRINT",EDGE,{"derivedFrom":subQ0}),1.0]])]});}
            var Q2;
            Q2=sQuery(id+"F14.wireOp",EDGE,"E54");
            revolve(context, id + "F15", {"operationType" : NewBodyOperationType.REMOVE, "surfaceOperationType" : NewSurfaceOperationType.NEW, "entities" : qUnion([Q0, Q1]), "axis" : qUnion([Q2]), "revolveType" : RevolveType.FULL, "oppositeDirection" : true});
        }
        {
            var Q0;
            {var subQ1=sQuery(id+"F0.wireOp",EDGE,"E25.2.0.1");Q0=makeQuery(id+"F0.imprint","IMPRINT",FACE,{"disambiguationData":[TD([[makeQuery(id+"F0.imprint","IMPRINT",EDGE,{"derivedFrom":subQ1}),1.0]])]});}
            extrude(context, id + "F16", {"entities" : qUnion([Q0]), "depth" : (38 - 2 * 6) * mm, "offsetDistance" : 25 * mm});
        }
        {
            var Q0;
            Q0=qCreatedBy(makeId("Top.planeOp"),FACE);
            var sketch = newSketch(context, id + "F17", { "sketchPlane" : qUnion([Q0])});
            skCircle(sketch, "E63", {"center": v(25, -30) * mm, "radius": 2 * mm});
            skLineSegment(sketch, "E64", {"start": v(23.68, -31.5) * mm, "end": v(26.32, -31.5) * mm});
            skSolve(sketch);
        }
        {
            var Q0;
            {var subQ0=sQuery(id+"F17.wireOp",EDGE,"E64");Q0=makeQuery(id+"F17.imprint","IMPRINT",FACE,{"disambiguationData":[TD([[makeQuery(id+"F17.imprint","IMPRINT",EDGE,{"derivedFrom":subQ0}),1.0]])]});}
            var Q1;
            {var subQ0=sQuery(id+"F17.wireOp",EDGE,"E64");Q1=makeQuery(id+"F17.imprint","IMPRINT",FACE,{"disambiguationData":[TD([[makeQuery(id+"F17.imprint","IMPRINT",EDGE,{"derivedFrom":subQ0}),-1.0]])]});}
            extrude(context, id + "F18", {"entities" : qUnion([Q0, Q1]), "depth" : 10 * mm, "offsetDistance" : 25 * mm});
        }
        {
            var Q0;
            Q0=makeQuery(id+"F18.opExtrude","CAP_FACE",FACE,{"disambiguationData":[OSD([sQuery(id+"F17.wireOp",EDGE,"E63")])],"isStart":false});
            var sketch = newSketch(context, id + "F19", { "sketchPlane" : qUnion([Q0])});
            skLineSegment(sketch, "E65.0", {"start": v(23.68, -31.5) * mm, "end": v(26.32, -31.5) * mm});
            skSolve(sketch);
        }
        {
            var Q0;
            {var subQ0=sQuery(id+"F19.wireOp",EDGE,"E65.0");Q0=makeQuery(id+"F19.imprint","IMPRINT",FACE,{"disambiguationData":[TD([[makeQuery(id+"F19.imprint","IMPRINT",EDGE,{"derivedFrom":subQ0}),-1.0]])]});}
            extrude(context, id + "F20", {"entities" : qUnion([Q0]), "operationType" : NewBodyOperationType.REMOVE, "oppositeDirection" : true, "depth" : 7 * mm, "offsetDistance" : 25 * mm});
        }
        {
            var Q0;
            Q0=makeQuery(id+"F18.opExtrude","CAP_EDGE",EDGE,{"disambiguationData":[OSD([sQuery(id+"F17.wireOp",EDGE,"E63")])],"isStart":false});
            chamfer(context, id + "F21", {"entities" : qUnion([Q0]), "width" : 0.5 * mm, "tangentPropagation" : true});
        }
        {
            var Q0;
            {var subQ0=sQuery(id+"F17.wireOp",EDGE,"E64");Q0=makeQuery(id+"F17.imprint","IMPRINT",FACE,{"disambiguationData":[TD([[makeQuery(id+"F17.imprint","IMPRINT",EDGE,{"derivedFrom":subQ0}),1.0]])]});}
            var Q1;
            {var subQ0=sQuery(id+"F17.wireOp",EDGE,"E64");Q1=makeQuery(id+"F17.imprint","IMPRINT",FACE,{"disambiguationData":[TD([[makeQuery(id+"F17.imprint","IMPRINT",EDGE,{"derivedFrom":subQ0}),-1.0]])]});}
            extrude(context, id + "F22", {"entities" : qUnion([Q0, Q1]), "operationType" : NewBodyOperationType.ADD, "oppositeDirection" : true, "depth" : 38 * mm, "offsetDistance" : 25 * mm});
        }
    });
